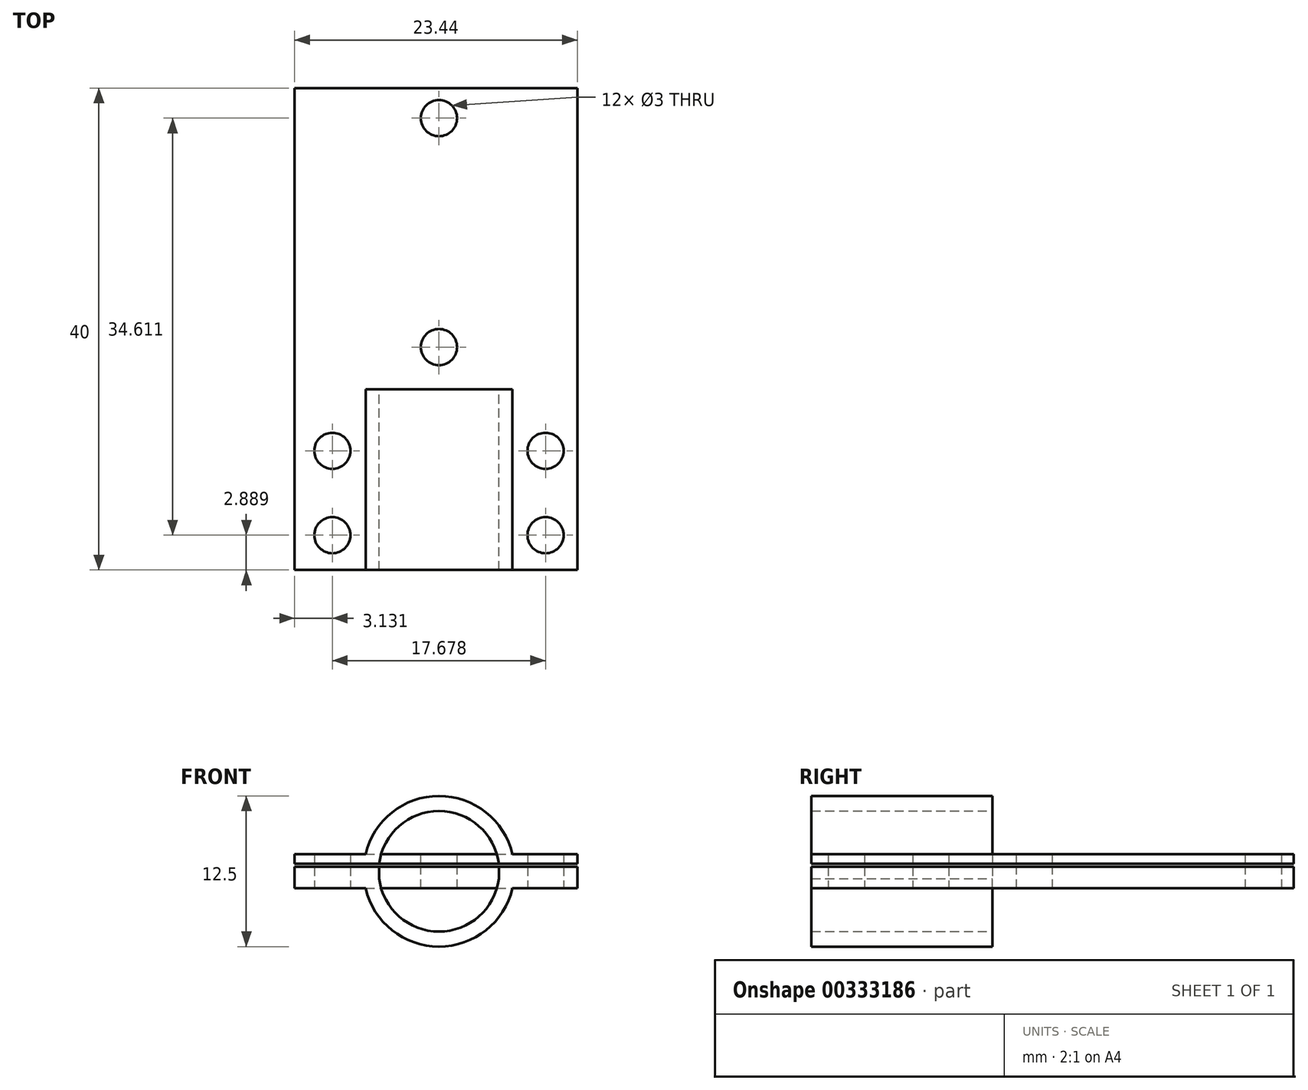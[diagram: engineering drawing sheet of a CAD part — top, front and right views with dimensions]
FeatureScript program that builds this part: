
annotation { "Feature Type Name" : "Feature", "Feature Type Description" : "" }
export const myFeature = defineFeature(function(context is Context, id is Id, definition is map)
    precondition{}
    {
        {
            var Q0;
            Q0=qCreatedBy(makeId("Front.planeOp"),FACE);
            var sketch = newSketch(context, id + "F0", { "sketchPlane" : qUnion([Q0])});
            skCircle(sketch, "E0", {"center": v(0, 0) * mm, "radius": 5 * mm});
            skArc(sketch, "E1", {"start": v(-6.09, -1.4) * mm, "mid": v(0, -6.25) * mm, "end": v(6.09, -1.4) * mm});
            skLineSegment(sketch, "E2.bottom", {"start": v(9.47, -1.4) * mm, "end": v(4.8, -1.4) * mm});
            skLineSegment(sketch, "E2.top", {"start": v(9.47, 1.4) * mm, "end": v(4.8, 1.4) * mm});
            skLineSegment(sketch, "E2.left", {"start": v(9.47, -1.4) * mm, "end": v(9.47, 1.4) * mm});
            skLineSegment(sketch, "E2.right", {"start": v(-9.47, -1.4) * mm, "end": v(-9.47, 1.4) * mm});
            skArc(sketch, "E3.trimOffspring", {"start": v(6.09, 1.4) * mm, "mid": v(0, 6.25) * mm, "end": v(-6.09, 1.4) * mm});
            skLineSegment(sketch, "E4.bottom", {"start": v(8.3, -0.63) * mm, "end": v(4.96, -0.63) * mm});
            skLineSegment(sketch, "E4.top", {"start": v(8.3, 0.63) * mm, "end": v(4.96, 0.63) * mm});
            skLineSegment(sketch, "E4.left", {"start": v(8.3, -0.63) * mm, "end": v(8.3, 0.63) * mm});
            skLineSegment(sketch, "E4.right", {"start": v(-8.3, -0.63) * mm, "end": v(-8.3, 0.63) * mm});
            skLineSegment(sketch, "E5.trimOffspring", {"start": v(-4.8, 1.4) * mm, "end": v(-9.47, 1.4) * mm});
            skLineSegment(sketch, "E6.trimOffspring", {"start": v(-4.96, 0.63) * mm, "end": v(-8.3, 0.63) * mm});
            skLineSegment(sketch, "E7.trimOffspring", {"start": v(-4.96, -0.63) * mm, "end": v(-8.3, -0.63) * mm});
            skLineSegment(sketch, "E8.trimOffspring", {"start": v(-4.8, -1.4) * mm, "end": v(-9.47, -1.4) * mm});
            skSolve(sketch);
        }
        {
            var Q0;
            Q0=qSketchRegion(id+"F0",true);
            extrude(context, id + "F1", {"entities" : qUnion([Q0]), "endBound" : BoundingType.SYMMETRIC, "depth" : 25 * mm});
        }
        {
            var Q0;
            Q0=makeQuery(id+"F1.opExtrude","SWEPT_FACE",FACE,{"disambiguationData":[OSD([sQuery(id+"F0.wireOp",EDGE,"E5.trimOffspring")])]});
            var sketch = newSketch(context, id + "F2", { "sketchPlane" : qUnion([Q0])});
            skLineSegment(sketch, "E9", {"start": v(-9.47, 0) * mm, "end": v(9.47, 0) * mm});
            skPoint(sketch, "E9.endSnap0", {"position": v(-9.47, 0) * mm});
            skLineSegment(sketch, "E10", {"start": v(9.47, 0) * mm, "end": v(9.47, 12.5) * mm});
            skLineSegment(sketch, "E11", {"start": v(9.47, 12.5) * mm, "end": v(-9.47, 12.5) * mm});
            skLineSegment(sketch, "E12", {"start": v(-9.47, 12.5) * mm, "end": v(-9.47, 0) * mm});
            skSolve(sketch);
        }
        {
            var Q0;
            Q0=qSketchRegion(id+"F2",true);
            extrude(context, id + "F3", {"entities" : qUnion([Q0]), "operationType" : NewBodyOperationType.ADD, "depth" : 5.1 * mm});
        }
        {
            var Q0;
            {var subQ3=sQuery(id+"F2.wireOp",EDGE,"E9");Q0=makeQuery(id+"F3.boolean.opBoolean","SPLIT",FACE,{"disambiguationData":[TD([makeQuery(id+"F3.opExtrude","CAP_FACE",FACE,{"disambiguationData":[OSD([subQ3,sQuery(id+"F2.wireOp",EDGE,"E10"),sQuery(id+"F2.wireOp",EDGE,"E11"),sQuery(id+"F2.wireOp",EDGE,"E12")])],"isStart":true})])],"derivedFrom":makeQuery(id+"F3.opExtrude","SWEPT_FACE",FACE,{"disambiguationData":[OSD([subQ3])]})});}
            extrude(context, id + "F4", {"entities" : qUnion([Q0]), "operationType" : NewBodyOperationType.REMOVE, "oppositeDirection" : true, "depth" : 25 * mm});
        }
        {
            var Q0;
            Q0=makeQuery(id+"F3.opExtrude","CAP_FACE",FACE,{"disambiguationData":[OSD([sQuery(id+"F2.wireOp",EDGE,"E9"),sQuery(id+"F2.wireOp",EDGE,"E10"),sQuery(id+"F2.wireOp",EDGE,"E11"),sQuery(id+"F2.wireOp",EDGE,"E12")])],"isStart":false});
            extrude(context, id + "F5", {"entities" : qUnion([Q0]), "operationType" : NewBodyOperationType.ADD, "oppositeDirection" : true, "depth" : 13 * mm});
        }
        {
            var Q0;
            {var subQ6=sQuery(id+"F0.wireOp",EDGE,"E4.bottom");var subQ9=sQuery(id+"F2.wireOp",EDGE,"E9");Q0=makeQuery(id+"F5.boolean.opBoolean","SPLIT",FACE,{"disambiguationData":[TD([makeQuery(id+"F1.opExtrude","SWEPT_FACE",FACE,{"disambiguationData":[OSD([subQ6])]})])],"derivedFrom":makeQuery(id+"F5.opExtrude","SWEPT_FACE",FACE,{"disambiguationData":[OSD([subQ9])]})});}
            extrude(context, id + "F6", {"entities" : qUnion([Q0]), "operationType" : NewBodyOperationType.REMOVE, "oppositeDirection" : true, "depth" : 3 * mm});
        }
        {
            var Q0;
            Q0=makeQuery(id+"F1.opExtrude","SWEPT_FACE",FACE,{"disambiguationData":[OSD([sQuery(id+"F0.wireOp",EDGE,"E2.bottom")])]});
            var sketch = newSketch(context, id + "F7", { "sketchPlane" : qUnion([Q0])});
            skCircle(sketch, "E13", {"center": v(8.84, 9.61) * mm, "radius": 1.5 * mm});
            skCircle(sketch, "E14.0.1.0", {"center": v(8.84, 2.61) * mm, "radius": 1.5 * mm});
            skLineSegment(sketch, "E14.direction1", {"start": v(8.84, 9.61) * mm, "end": v(33.84, 9.61) * mm, "construction": true});
            skLineSegment(sketch, "E14.direction2", {"start": v(8.84, 9.61) * mm, "end": v(8.84, 2.61) * mm, "construction": true});
            skCircle(sketch, "E15.MirrorC", {"center": v(-8.84, 9.61) * mm, "radius": 1.5 * mm});
            skCircle(sketch, "E16.MirrorC", {"center": v(-8.84, 2.61) * mm, "radius": 1.5 * mm});
            skSolve(sketch);
        }
        {
            var Q0;
            Q0=makeQuery(id+"F1.opExtrude","SWEPT_FACE",FACE,{"disambiguationData":[OSD([sQuery(id+"F0.wireOp",EDGE,"E2.left")])]});
            extrude(context, id + "F8", {"entities" : qUnion([Q0]), "operationType" : NewBodyOperationType.ADD, "depth" : 2 * mm});
        }
        {
            var Q0;
            {var subQ0=sQuery(id+"F0.wireOp",EDGE,"E4.left");Q0=makeQuery(id+"F6.boolean.opBoolean","MERGE",FACE,{"derivedFrom":[makeQuery(id+"F1.opExtrude","SWEPT_FACE",FACE,{"disambiguationData":[OSD([subQ0])]}),makeQuery(id+"F6.opExtrude","SWEPT_FACE",FACE,{"disambiguationData":[OSD([subQ0,sQuery(id+"F2.wireOp",EDGE,"E9")])]})]});}
            extrude(context, id + "F9", {"entities" : qUnion([Q0]), "operationType" : NewBodyOperationType.REMOVE, "oppositeDirection" : true, "depth" : 23.6 * mm});
        }
        {
            var Q0;
            {var subQ0=sQuery(id+"F2.wireOp",EDGE,"E12");Q0=makeQuery(id+"F5.boolean.opBoolean","MERGE",FACE,{"derivedFrom":[makeQuery(id+"F3.boolean.opBoolean","MERGE",FACE,{"derivedFrom":[makeQuery(id+"F1.opExtrude","SWEPT_FACE",FACE,{"disambiguationData":[OSD([sQuery(id+"F0.wireOp",EDGE,"E2.right")])]}),makeQuery(id+"F3.opExtrude","SWEPT_FACE",FACE,{"disambiguationData":[OSD([subQ0])]})]}),makeQuery(id+"F5.opExtrude","SWEPT_FACE",FACE,{"disambiguationData":[OSD([subQ0])]})]});}
            var sketch = newSketch(context, id + "F10", { "sketchPlane" : qUnion([Q0])});
            skLineSegment(sketch, "E17", {"start": v(0, -1.4) * mm, "end": v(0, 1.4) * mm});
            skSolve(sketch);
        }
        {
            var Q0;
            Q0=qSketchRegion(id+"F10",true);
            var Q1;
            Q1=makeQuery(id+"F10.imprint","IMPRINT",FACE,{"disambiguationData":[TD([[makeQuery(id+"F10.imprint","IMPRINT",EDGE,{"derivedFrom":sQuery(id+"F10.wireOp",EDGE,"E17")}),-1.0]])]});
            extrude(context, id + "F11", {"entities" : qUnion([Q0, Q1]), "operationType" : NewBodyOperationType.ADD, "depth" : 2.5 * mm});
        }
        {
            var Q0;
            {var subQ0=sQuery(id+"F0.wireOp",EDGE,"E4.right");Q0=makeQuery(id+"F6.boolean.opBoolean","MERGE",FACE,{"derivedFrom":[makeQuery(id+"F1.opExtrude","SWEPT_FACE",FACE,{"disambiguationData":[OSD([subQ0])]}),makeQuery(id+"F6.opExtrude","SWEPT_FACE",FACE,{"disambiguationData":[OSD([subQ0,sQuery(id+"F2.wireOp",EDGE,"E9")])]})]});}
            extrude(context, id + "F12", {"entities" : qUnion([Q0]), "operationType" : NewBodyOperationType.REMOVE, "oppositeDirection" : true, "depth" : 2.5 * mm});
        }
        {
            var Q0;
            Q0=makeQuery(id+"F11.opExtrude","SWEPT_FACE",FACE,{"disambiguationData":[OSD([sQuery(id+"F10.wireOp",EDGE,"E17")])]});
            extrude(context, id + "F13", {"entities" : qUnion([Q0]), "operationType" : NewBodyOperationType.ADD, "depth" : 12.5 * mm});
        }
        {
            var Q0;
            {var subQ4=sQuery(id+"F0.wireOp",EDGE,"E6.trimOffspring");var subQ7=sQuery(id+"F0.wireOp",EDGE,"E2.right");var subQ9=sQuery(id+"F2.wireOp",EDGE,"E12");Q0=makeQuery(id+"F13.boolean.opBoolean","SPLIT",FACE,{"disambiguationData":[TD([makeQuery(id+"F1.opExtrude","SWEPT_FACE",FACE,{"disambiguationData":[OSD([subQ4])]})])],"derivedFrom":makeQuery(id+"F5.boolean.opBoolean","MERGE",FACE,{"derivedFrom":[makeQuery(id+"F3.boolean.opBoolean","MERGE",FACE,{"derivedFrom":[makeQuery(id+"F1.opExtrude","SWEPT_FACE",FACE,{"disambiguationData":[OSD([subQ7])]}),makeQuery(id+"F3.opExtrude","SWEPT_FACE",FACE,{"disambiguationData":[OSD([subQ9])]})]}),makeQuery(id+"F5.opExtrude","SWEPT_FACE",FACE,{"disambiguationData":[OSD([subQ9])]})]})});}
            extrude(context, id + "F14", {"entities" : qUnion([Q0]), "operationType" : NewBodyOperationType.ADD, "depth" : 2 * mm});
        }
        {
            var Q0;
            Q0=qSketchRegion(id+"F7",true);
            extrude(context, id + "F15", {"entities" : qUnion([Q0]), "operationType" : NewBodyOperationType.REMOVE, "oppositeDirection" : true, "depth" : 25 * mm});
        }
        {
            var Q0;
            {var subQ2=sQuery(id+"F2.wireOp",EDGE,"E9");Q0=makeQuery(id+"F5.boolean.opBoolean","SPLIT",FACE,{"disambiguationData":[TD([makeQuery(id+"F1.opExtrude","SWEPT_FACE",FACE,{"disambiguationData":[OSD([sQuery(id+"F0.wireOp",EDGE,"E1")])]})])],"derivedFrom":makeQuery(id+"F5.opExtrude","SWEPT_FACE",FACE,{"disambiguationData":[OSD([subQ2])]})});}
            var Q1;
            {var subQ2=sQuery(id+"F2.wireOp",EDGE,"E9");Q1=makeQuery(id+"F3.boolean.opBoolean","SPLIT",FACE,{"disambiguationData":[TD([makeQuery(id+"F1.opExtrude","SWEPT_FACE",FACE,{"disambiguationData":[OSD([sQuery(id+"F0.wireOp",EDGE,"E2.top")])]})])],"derivedFrom":makeQuery(id+"F3.opExtrude","SWEPT_FACE",FACE,{"disambiguationData":[OSD([subQ2])]})});}
            extrude(context, id + "F16", {"entities" : qUnion([Q0, Q1]), "operationType" : NewBodyOperationType.REMOVE, "oppositeDirection" : true, "depth" : 2 * mm});
        }
        {
            var Q0;
            {var subQ0=sQuery(id+"F2.wireOp",EDGE,"E9");var subQ1=sQuery(id+"F0.wireOp",EDGE,"E4.right");Q0=makeQuery(id+"F13.boolean.opBoolean","MERGE",FACE,{"derivedFrom":[makeQuery(id+"F12.boolean.opBoolean","COPY",FACE,{"derivedFrom":makeQuery(id+"F12.opExtrude","CAP_FACE",FACE,{"disambiguationData":[OSD([subQ1,subQ0])],"isStart":false})}),makeQuery(id+"F13.opExtrude","SWEPT_FACE",FACE,{"disambiguationData":[OSD([subQ1,subQ0,sQuery(id+"F10.wireOp",EDGE,"E17")])]})]});}
            extrude(context, id + "F17", {"entities" : qUnion([Q0]), "operationType" : NewBodyOperationType.REMOVE, "oppositeDirection" : true, "depth" : 12 * mm});
        }
        {
            var Q0;
            {var subQ0=sQuery(id+"F2.wireOp",EDGE,"E12");var subQ1=sQuery(id+"F2.wireOp",EDGE,"E9");var subQ2=sQuery(id+"F0.wireOp",EDGE,"E4.right");var subQ3=sQuery(id+"F0.wireOp",EDGE,"E2.right");Q0=makeQuery(id+"F17.boolean.opBoolean","MERGE",FACE,{"derivedFrom":[makeQuery(id+"F14.boolean.opBoolean","MERGE",FACE,{"derivedFrom":[makeQuery(id+"F12.boolean.opBoolean","MERGE",FACE,{"derivedFrom":[makeQuery(id+"F9.boolean.opBoolean","MERGE",FACE,{"derivedFrom":[makeQuery(id+"F6.boolean.opBoolean","COPY",FACE,{"derivedFrom":makeQuery(id+"F6.opExtrude","CAP_FACE",FACE,{"disambiguationData":[OSD([subQ1])],"isStart":false})}),makeQuery(id+"F9.opExtrude","SWEPT_FACE",FACE,{"disambiguationData":[OSD([sQuery(id+"F0.wireOp",EDGE,"E4.left"),subQ1])]})]}),makeQuery(id+"F12.opExtrude","SWEPT_FACE",FACE,{"disambiguationData":[OSD([subQ2,subQ1])]})]}),makeQuery(id+"F14.opExtrude","SWEPT_FACE",FACE,{"disambiguationData":[OSD([subQ3,subQ2,subQ1,subQ0])]})]}),makeQuery(id+"F17.opExtrude","SWEPT_FACE",FACE,{"disambiguationData":[OSD([subQ3,subQ2,subQ1,subQ0,sQuery(id+"F10.wireOp",EDGE,"E17")])]})]});}
            extrude(context, id + "F18", {"entities" : qUnion([Q0]), "operationType" : NewBodyOperationType.REMOVE, "oppositeDirection" : true, "depth" : 25 * mm});
        }
        {
            var Q0;
            {var subQ2=sQuery(id+"F2.wireOp",EDGE,"E9");Q0=makeQuery(id+"F16.boolean.opBoolean","COPY",FACE,{"derivedFrom":makeQuery(id+"F16.opExtrude","CAP_FACE",FACE,{"disambiguationData":[OSD([subQ2]),TDD([makeQuery(id+"F5.boolean.opBoolean","SPLIT",FACE,{"disambiguationData":[TD([makeQuery(id+"F1.opExtrude","SWEPT_FACE",FACE,{"disambiguationData":[OSD([sQuery(id+"F0.wireOp",EDGE,"E1")])]})])],"derivedFrom":makeQuery(id+"F5.opExtrude","SWEPT_FACE",FACE,{"disambiguationData":[OSD([subQ2])]})})])],"isStart":false})});}
            extrude(context, id + "F19", {"entities" : qUnion([Q0]), "operationType" : NewBodyOperationType.REMOVE, "oppositeDirection" : true, "depth" : 25 * mm});
        }
        {
            var Q0;
            {var subQ2=sQuery(id+"F2.wireOp",EDGE,"E9");Q0=makeQuery(id+"F16.boolean.opBoolean","COPY",FACE,{"derivedFrom":makeQuery(id+"F16.opExtrude","CAP_FACE",FACE,{"disambiguationData":[OSD([subQ2]),TDD([makeQuery(id+"F3.boolean.opBoolean","SPLIT",FACE,{"disambiguationData":[TD([makeQuery(id+"F1.opExtrude","SWEPT_FACE",FACE,{"disambiguationData":[OSD([sQuery(id+"F0.wireOp",EDGE,"E2.top")])]})])],"derivedFrom":makeQuery(id+"F3.opExtrude","SWEPT_FACE",FACE,{"disambiguationData":[OSD([subQ2])]})})])],"isStart":false})});}
            extrude(context, id + "F20", {"entities" : qUnion([Q0]), "operationType" : NewBodyOperationType.REMOVE, "oppositeDirection" : true, "depth" : 25 * mm});
        }
        {
            var Q0;
            {var subQ0=sQuery(id+"F10.wireOp",EDGE,"E17");var subQ1=sQuery(id+"F2.wireOp",EDGE,"E9");var subQ2=sQuery(id+"F0.wireOp",EDGE,"E7.trimOffspring");var subQ3=sQuery(id+"F0.wireOp",EDGE,"E4.right");Q0=makeQuery(id+"F18.boolean.opBoolean","MERGE",FACE,{"derivedFrom":[makeQuery(id+"F17.boolean.opBoolean","MERGE",FACE,{"derivedFrom":[makeQuery(id+"F13.boolean.opBoolean","MERGE",FACE,{"derivedFrom":[makeQuery(id+"F12.boolean.opBoolean","MERGE",FACE,{"derivedFrom":[makeQuery(id+"F6.boolean.opBoolean","MERGE",FACE,{"derivedFrom":[makeQuery(id+"F1.opExtrude","SWEPT_FACE",FACE,{"disambiguationData":[OSD([subQ2])]}),makeQuery(id+"F6.opExtrude","SWEPT_FACE",FACE,{"disambiguationData":[OSD([subQ2,subQ1])]})]}),makeQuery(id+"F12.opExtrude","SWEPT_FACE",FACE,{"disambiguationData":[OSD([subQ3,subQ2,subQ1])]})]}),makeQuery(id+"F13.opExtrude","SWEPT_FACE",FACE,{"disambiguationData":[OSD([subQ3,subQ2,subQ1,subQ0])]})]}),makeQuery(id+"F17.opExtrude","SWEPT_FACE",FACE,{"disambiguationData":[OSD([subQ3,subQ2,subQ1,subQ0])]})]}),makeQuery(id+"F18.opExtrude","SWEPT_FACE",FACE,{"disambiguationData":[OSD([sQuery(id+"F0.wireOp",EDGE,"E2.right"),subQ3,subQ2,subQ1,sQuery(id+"F2.wireOp",EDGE,"E12"),subQ0])]})]});}
            extrude(context, id + "F21", {"entities" : qUnion([Q0]), "operationType" : NewBodyOperationType.ADD, "depth" : 1 * mm});
        }
        {
            var Q0;
            {var subQ0=sQuery(id+"F2.wireOp",EDGE,"E9");var subQ1=sQuery(id+"F0.wireOp",EDGE,"E4.left");var subQ2=sQuery(id+"F0.wireOp",EDGE,"E4.bottom");Q0=makeQuery(id+"F18.boolean.opBoolean","MERGE",FACE,{"derivedFrom":[makeQuery(id+"F9.boolean.opBoolean","MERGE",FACE,{"derivedFrom":[makeQuery(id+"F6.boolean.opBoolean","MERGE",FACE,{"derivedFrom":[makeQuery(id+"F1.opExtrude","SWEPT_FACE",FACE,{"disambiguationData":[OSD([subQ2])]}),makeQuery(id+"F6.opExtrude","SWEPT_FACE",FACE,{"disambiguationData":[OSD([subQ2,subQ0])]})]}),makeQuery(id+"F9.opExtrude","SWEPT_FACE",FACE,{"disambiguationData":[OSD([subQ2,subQ1,subQ0])]})]}),makeQuery(id+"F18.opExtrude","SWEPT_FACE",FACE,{"disambiguationData":[OSD([subQ2,subQ1,subQ0])]})]});}
            extrude(context, id + "F22", {"entities" : qUnion([Q0]), "operationType" : NewBodyOperationType.ADD, "depth" : 1 * mm});
        }
        {
            var Q0;
            {var subQ0=sQuery(id+"F10.wireOp",EDGE,"E17");var subQ1=sQuery(id+"F2.wireOp",EDGE,"E12");var subQ2=sQuery(id+"F2.wireOp",EDGE,"E11");var subQ3=sQuery(id+"F2.wireOp",EDGE,"E9");var subQ4=sQuery(id+"F0.wireOp",EDGE,"E8.trimOffspring");var subQ5=sQuery(id+"F0.wireOp",EDGE,"E7.trimOffspring");var subQ6=sQuery(id+"F0.wireOp",EDGE,"E6.trimOffspring");var subQ7=sQuery(id+"F0.wireOp",EDGE,"E5.trimOffspring");var subQ8=sQuery(id+"F0.wireOp",EDGE,"E4.right");var subQ9=sQuery(id+"F0.wireOp",EDGE,"E4.left");var subQ10=sQuery(id+"F0.wireOp",EDGE,"E4.top");var subQ11=sQuery(id+"F0.wireOp",EDGE,"E4.bottom");var subQ12=sQuery(id+"F0.wireOp",EDGE,"E3.trimOffspring");var subQ13=sQuery(id+"F0.wireOp",EDGE,"E2.right");var subQ14=sQuery(id+"F0.wireOp",EDGE,"E2.left");var subQ15=sQuery(id+"F0.wireOp",EDGE,"E2.top");var subQ16=sQuery(id+"F0.wireOp",EDGE,"E2.bottom");var subQ17=sQuery(id+"F0.wireOp",EDGE,"E1");var subQ18=sQuery(id+"F0.wireOp",EDGE,"E0");Q0=makeQuery(id+"F22.boolean.opBoolean","MERGE",FACE,{"derivedFrom":[makeQuery(id+"F21.boolean.opBoolean","MERGE",FACE,{"derivedFrom":[makeQuery(id+"F18.boolean.opBoolean","SPLIT",FACE,{"disambiguationData":[TD([makeQuery(id+"F1.opExtrude","SWEPT_FACE",FACE,{"disambiguationData":[OSD([subQ16])]})])],"derivedFrom":makeQuery(id+"F14.boolean.opBoolean","MERGE",FACE,{"derivedFrom":[makeQuery(id+"F13.boolean.opBoolean","MERGE",FACE,{"derivedFrom":[makeQuery(id+"F8.boolean.opBoolean","MERGE",FACE,{"derivedFrom":[makeQuery(id+"F5.boolean.opBoolean","MERGE",FACE,{"derivedFrom":[makeQuery(id+"F3.boolean.opBoolean","MERGE",FACE,{"derivedFrom":[makeQuery(id+"F1.opExtrude","CAP_FACE",FACE,{"disambiguationData":[OSD([subQ18,subQ17,subQ16,subQ15,subQ14,subQ13,subQ12,subQ11,subQ10,subQ9,subQ8,subQ7,subQ6,subQ5,subQ4])],"isStart":true}),makeQuery(id+"F3.opExtrude","SWEPT_FACE",FACE,{"disambiguationData":[OSD([subQ2])]})]}),makeQuery(id+"F5.opExtrude","SWEPT_FACE",FACE,{"disambiguationData":[OSD([subQ2])]})]}),makeQuery(id+"F8.opExtrude","SWEPT_FACE",FACE,{"disambiguationData":[OSD([subQ14]),TDD([makeQuery(id+"F1.opExtrude","CAP_EDGE",EDGE,{"disambiguationData":[OSD([subQ14])],"isStart":true})])]})]}),makeQuery(id+"F13.opExtrude","CAP_FACE",FACE,{"disambiguationData":[OSD([subQ0])],"isStart":false})]}),makeQuery(id+"F14.opExtrude","SWEPT_FACE",FACE,{"disambiguationData":[OSD([subQ13,subQ2,subQ1])]})]})}),makeQuery(id+"F21.opExtrude","SWEPT_FACE",FACE,{"disambiguationData":[OSD([subQ18,subQ17,subQ16,subQ15,subQ14,subQ13,subQ12,subQ11,subQ10,subQ9,subQ8,subQ7,subQ6,subQ5,subQ4,subQ3,subQ2,subQ1,subQ0])]})]}),makeQuery(id+"F22.opExtrude","SWEPT_FACE",FACE,{"disambiguationData":[OSD([subQ18,subQ17,subQ16,subQ15,subQ14,subQ13,subQ12,subQ11,subQ10,subQ9,subQ8,subQ7,subQ6,subQ5,subQ4,subQ3,subQ2,subQ1,subQ0])]})]});}
            var Q1;
            {var subQ0=sQuery(id+"F10.wireOp",EDGE,"E17");var subQ1=sQuery(id+"F0.wireOp",EDGE,"E8.trimOffspring");var subQ2=sQuery(id+"F0.wireOp",EDGE,"E5.trimOffspring");var subQ3=sQuery(id+"F0.wireOp",EDGE,"E2.right");var subQ5=sQuery(id+"F0.wireOp",EDGE,"E2.left");var subQ6=sQuery(id+"F0.wireOp",EDGE,"E2.top");var subQ8=sQuery(id+"F0.wireOp",EDGE,"E0");var subQ11=sQuery(id+"F0.wireOp",EDGE,"E6.trimOffspring");var subQ13=sQuery(id+"F0.wireOp",EDGE,"E4.top");var subQ16=sQuery(id+"F2.wireOp",EDGE,"E12");var subQ18=sQuery(id+"F0.wireOp",EDGE,"E4.right");var subQ19=makeQuery(id+"F1.opExtrude","SWEPT_FACE",FACE,{"disambiguationData":[OSD([subQ6])]});var subQ20=sQuery(id+"F2.wireOp",EDGE,"E11");var subQ21=sQuery(id+"F0.wireOp",EDGE,"E4.left");Q1=makeQuery(id+"F18.boolean.opBoolean","SPLIT",FACE,{"disambiguationData":[TD([subQ19])],"derivedFrom":makeQuery(id+"F14.boolean.opBoolean","MERGE",FACE,{"derivedFrom":[makeQuery(id+"F13.boolean.opBoolean","MERGE",FACE,{"derivedFrom":[makeQuery(id+"F8.boolean.opBoolean","MERGE",FACE,{"derivedFrom":[makeQuery(id+"F5.boolean.opBoolean","MERGE",FACE,{"derivedFrom":[makeQuery(id+"F3.boolean.opBoolean","MERGE",FACE,{"derivedFrom":[makeQuery(id+"F1.opExtrude","CAP_FACE",FACE,{"disambiguationData":[OSD([subQ8,sQuery(id+"F0.wireOp",EDGE,"E1"),sQuery(id+"F0.wireOp",EDGE,"E2.bottom"),subQ6,subQ5,subQ3,sQuery(id+"F0.wireOp",EDGE,"E3.trimOffspring"),sQuery(id+"F0.wireOp",EDGE,"E4.bottom"),subQ13,subQ21,subQ18,subQ2,subQ11,sQuery(id+"F0.wireOp",EDGE,"E7.trimOffspring"),subQ1])],"isStart":true}),makeQuery(id+"F3.opExtrude","SWEPT_FACE",FACE,{"disambiguationData":[OSD([subQ20])]})]}),makeQuery(id+"F5.opExtrude","SWEPT_FACE",FACE,{"disambiguationData":[OSD([subQ20])]})]}),makeQuery(id+"F8.opExtrude","SWEPT_FACE",FACE,{"disambiguationData":[OSD([subQ5]),TDD([makeQuery(id+"F1.opExtrude","CAP_EDGE",EDGE,{"disambiguationData":[OSD([subQ5])],"isStart":true})])]})]}),makeQuery(id+"F13.opExtrude","CAP_FACE",FACE,{"disambiguationData":[OSD([subQ0])],"isStart":false})]}),makeQuery(id+"F14.opExtrude","SWEPT_FACE",FACE,{"disambiguationData":[OSD([subQ3,subQ20,subQ16])]})]})});}
            extrude(context, id + "F23", {"entities" : qUnion([Q0, Q1]), "operationType" : NewBodyOperationType.REMOVE, "oppositeDirection" : true, "depth" : 10 * mm});
        }
        {
            var Q0;
            Q0=makeQuery(id+"F23.boolean.opBoolean","COPY",FACE,{"derivedFrom":makeQuery(id+"F23.opExtrude","CAP_FACE",FACE,{"disambiguationData":[OSD([sQuery(id+"F0.wireOp",EDGE,"E0"),sQuery(id+"F0.wireOp",EDGE,"E1"),sQuery(id+"F0.wireOp",EDGE,"E2.bottom"),sQuery(id+"F0.wireOp",EDGE,"E2.top"),sQuery(id+"F0.wireOp",EDGE,"E2.left"),sQuery(id+"F0.wireOp",EDGE,"E2.right"),sQuery(id+"F0.wireOp",EDGE,"E3.trimOffspring"),sQuery(id+"F0.wireOp",EDGE,"E4.bottom"),sQuery(id+"F0.wireOp",EDGE,"E4.top"),sQuery(id+"F0.wireOp",EDGE,"E4.left"),sQuery(id+"F0.wireOp",EDGE,"E4.right"),sQuery(id+"F0.wireOp",EDGE,"E5.trimOffspring"),sQuery(id+"F0.wireOp",EDGE,"E6.trimOffspring"),sQuery(id+"F0.wireOp",EDGE,"E7.trimOffspring"),sQuery(id+"F0.wireOp",EDGE,"E8.trimOffspring"),sQuery(id+"F2.wireOp",EDGE,"E9"),sQuery(id+"F2.wireOp",EDGE,"E11"),sQuery(id+"F2.wireOp",EDGE,"E12"),sQuery(id+"F10.wireOp",EDGE,"E17")])],"isStart":false})});
            var sketch = newSketch(context, id + "F24", { "sketchPlane" : qUnion([Q0])});
            skLineSegment(sketch, "E18.bottom", {"start": v(11.97, 0.37) * mm, "end": v(-11.47, 0.37) * mm});
            skLineSegment(sketch, "E18.top", {"start": v(11.97, -1.4) * mm, "end": v(-11.47, -1.4) * mm});
            skLineSegment(sketch, "E18.left", {"start": v(11.97, 0.37) * mm, "end": v(11.97, -1.4) * mm});
            skLineSegment(sketch, "E18.right", {"start": v(-11.47, 0.37) * mm, "end": v(-11.47, -1.4) * mm});
            skSolve(sketch);
        }
        {
            var Q0;
            Q0=qSketchRegion(id+"F24",true);
            extrude(context, id + "F25", {"entities" : qUnion([Q0]), "operationType" : NewBodyOperationType.ADD, "depth" : 25 * mm});
        }
        {
            var Q0;
            Q0=makeQuery(id+"F23.boolean.opBoolean","COPY",FACE,{"derivedFrom":makeQuery(id+"F23.opExtrude","CAP_FACE",FACE,{"disambiguationData":[OSD([sQuery(id+"F0.wireOp",EDGE,"E0"),sQuery(id+"F0.wireOp",EDGE,"E1"),sQuery(id+"F0.wireOp",EDGE,"E2.bottom"),sQuery(id+"F0.wireOp",EDGE,"E2.top"),sQuery(id+"F0.wireOp",EDGE,"E2.left"),sQuery(id+"F0.wireOp",EDGE,"E2.right"),sQuery(id+"F0.wireOp",EDGE,"E3.trimOffspring"),sQuery(id+"F0.wireOp",EDGE,"E4.bottom"),sQuery(id+"F0.wireOp",EDGE,"E4.top"),sQuery(id+"F0.wireOp",EDGE,"E4.left"),sQuery(id+"F0.wireOp",EDGE,"E4.right"),sQuery(id+"F0.wireOp",EDGE,"E5.trimOffspring"),sQuery(id+"F0.wireOp",EDGE,"E6.trimOffspring"),sQuery(id+"F0.wireOp",EDGE,"E7.trimOffspring"),sQuery(id+"F0.wireOp",EDGE,"E8.trimOffspring"),sQuery(id+"F2.wireOp",EDGE,"E11"),sQuery(id+"F2.wireOp",EDGE,"E12"),sQuery(id+"F10.wireOp",EDGE,"E17")])],"isStart":false})});
            var sketch = newSketch(context, id + "F26", { "sketchPlane" : qUnion([Q0])});
            skLineSegment(sketch, "E19.bottom", {"start": v(11.97, 0.63) * mm, "end": v(-11.47, 0.63) * mm});
            skLineSegment(sketch, "E19.top", {"start": v(11.97, 1.4) * mm, "end": v(-11.47, 1.4) * mm});
            skLineSegment(sketch, "E19.left", {"start": v(11.97, 0.63) * mm, "end": v(11.97, 1.4) * mm});
            skLineSegment(sketch, "E19.right", {"start": v(-11.47, 0.63) * mm, "end": v(-11.47, 1.4) * mm});
            skSolve(sketch);
        }
        {
            var Q0;
            Q0=qSketchRegion(id+"F26",true);
            extrude(context, id + "F27", {"entities" : qUnion([Q0]), "operationType" : NewBodyOperationType.ADD, "depth" : 25 * mm});
        }
        {
            var Q0;
            {var subQ0=sQuery(id+"F0.wireOp",EDGE,"E5.trimOffspring");var subQ1=makeQuery(id+"F1.opExtrude","SWEPT_FACE",FACE,{"disambiguationData":[OSD([subQ0])]});var subQ2=sQuery(id+"F2.wireOp",EDGE,"E9");var subQ4=makeQuery(id+"F3.opExtrude","CAP_EDGE",EDGE,{"disambiguationData":[OSD([subQ2])],"isStart":true});var subQ5=makeQuery(id+"F3.boolean.opBoolean","SPLIT",EDGE,{"disambiguationData":[topologyDisambiguationEdgeConnected([subQ1])],"derivedFrom":subQ4});var subQ6=sQuery(id+"F0.wireOp",EDGE,"E2.right");var subQ7=sQuery(id+"F0.wireOp",EDGE,"E2.top");var subQ8=makeQuery(id+"F1.opExtrude","SWEPT_FACE",FACE,{"disambiguationData":[OSD([subQ7])]});var subQ9=makeQuery(id+"F3.boolean.opBoolean","SPLIT",EDGE,{"disambiguationData":[topologyDisambiguationEdgeConnected([subQ8])],"derivedFrom":subQ4});Q0=makeQuery(id+"F27.boolean.opBoolean","MERGE",FACE,{"derivedFrom":[makeQuery(id+"F20.boolean.opBoolean","MERGE",FACE,{"derivedFrom":[makeQuery(id+"F16.boolean.opBoolean","MERGE",FACE,{"derivedFrom":[makeQuery(id+"F8.boolean.opBoolean","MERGE",FACE,{"derivedFrom":[subQ8,makeQuery(id+"F8.opExtrude","SWEPT_FACE",FACE,{"disambiguationData":[OSD([subQ7,sQuery(id+"F0.wireOp",EDGE,"E2.left"),sQuery(id+"F2.wireOp",EDGE,"E10")])]})]}),makeQuery(id+"F16.opExtrude","SWEPT_FACE",FACE,{"disambiguationData":[OSD([subQ2]),TDD([subQ9])]})]}),makeQuery(id+"F20.opExtrude","SWEPT_FACE",FACE,{"disambiguationData":[OSD([subQ2]),TDD([makeQuery(id+"F16.boolean.opBoolean","COPY",EDGE,{"derivedFrom":makeQuery(id+"F16.opExtrude","CAP_EDGE",EDGE,{"disambiguationData":[OSD([subQ2]),TDD([subQ9])],"isStart":false})})])]})]}),makeQuery(id+"F20.boolean.opBoolean","MERGE",FACE,{"derivedFrom":[makeQuery(id+"F16.boolean.opBoolean","MERGE",FACE,{"derivedFrom":[makeQuery(id+"F13.boolean.opBoolean","MERGE",FACE,{"derivedFrom":[makeQuery(id+"F11.boolean.opBoolean","MERGE",FACE,{"derivedFrom":[subQ1,makeQuery(id+"F11.opExtrude","SWEPT_FACE",FACE,{"disambiguationData":[OSD([subQ6,subQ0])]})]}),makeQuery(id+"F13.opExtrude","SWEPT_FACE",FACE,{"disambiguationData":[OSD([subQ6,subQ0,subQ2,sQuery(id+"F2.wireOp",EDGE,"E12"),sQuery(id+"F10.wireOp",EDGE,"E17")])]})]}),makeQuery(id+"F16.opExtrude","SWEPT_FACE",FACE,{"disambiguationData":[OSD([subQ2]),TDD([subQ5])]})]}),makeQuery(id+"F20.opExtrude","SWEPT_FACE",FACE,{"disambiguationData":[OSD([subQ2]),TDD([makeQuery(id+"F16.boolean.opBoolean","COPY",EDGE,{"derivedFrom":makeQuery(id+"F16.opExtrude","CAP_EDGE",EDGE,{"disambiguationData":[OSD([subQ2]),TDD([subQ5])],"isStart":false})})])]})]}),makeQuery(id+"F27.opExtrude","SWEPT_FACE",FACE,{"disambiguationData":[OSD([sQuery(id+"F26.wireOp",EDGE,"E19.top")])]})]});}
            var sketch = newSketch(context, id + "F28", { "sketchPlane" : qUnion([Q0])});
            skCircle(sketch, "E20", {"center": v(0, 6) * mm, "radius": 1.5 * mm});
            skPoint(sketch, "E20.centerSnap0", {"position": v(0, 2.5) * mm});
            skCircle(sketch, "E21.0.1.0", {"center": v(0, 25) * mm, "radius": 1.5 * mm});
            skLineSegment(sketch, "E21.direction1", {"start": v(0, 6) * mm, "end": v(25, 6) * mm, "construction": true});
            skLineSegment(sketch, "E21.direction2", {"start": v(0, 6) * mm, "end": v(0, 25) * mm, "construction": true});
            skSolve(sketch);
        }
        {
            var Q0;
            Q0=qSketchRegion(id+"F28",true);
            extrude(context, id + "F29", {"entities" : qUnion([Q0]), "operationType" : NewBodyOperationType.REMOVE, "oppositeDirection" : true, "depth" : 25 * mm});
        }
    });
